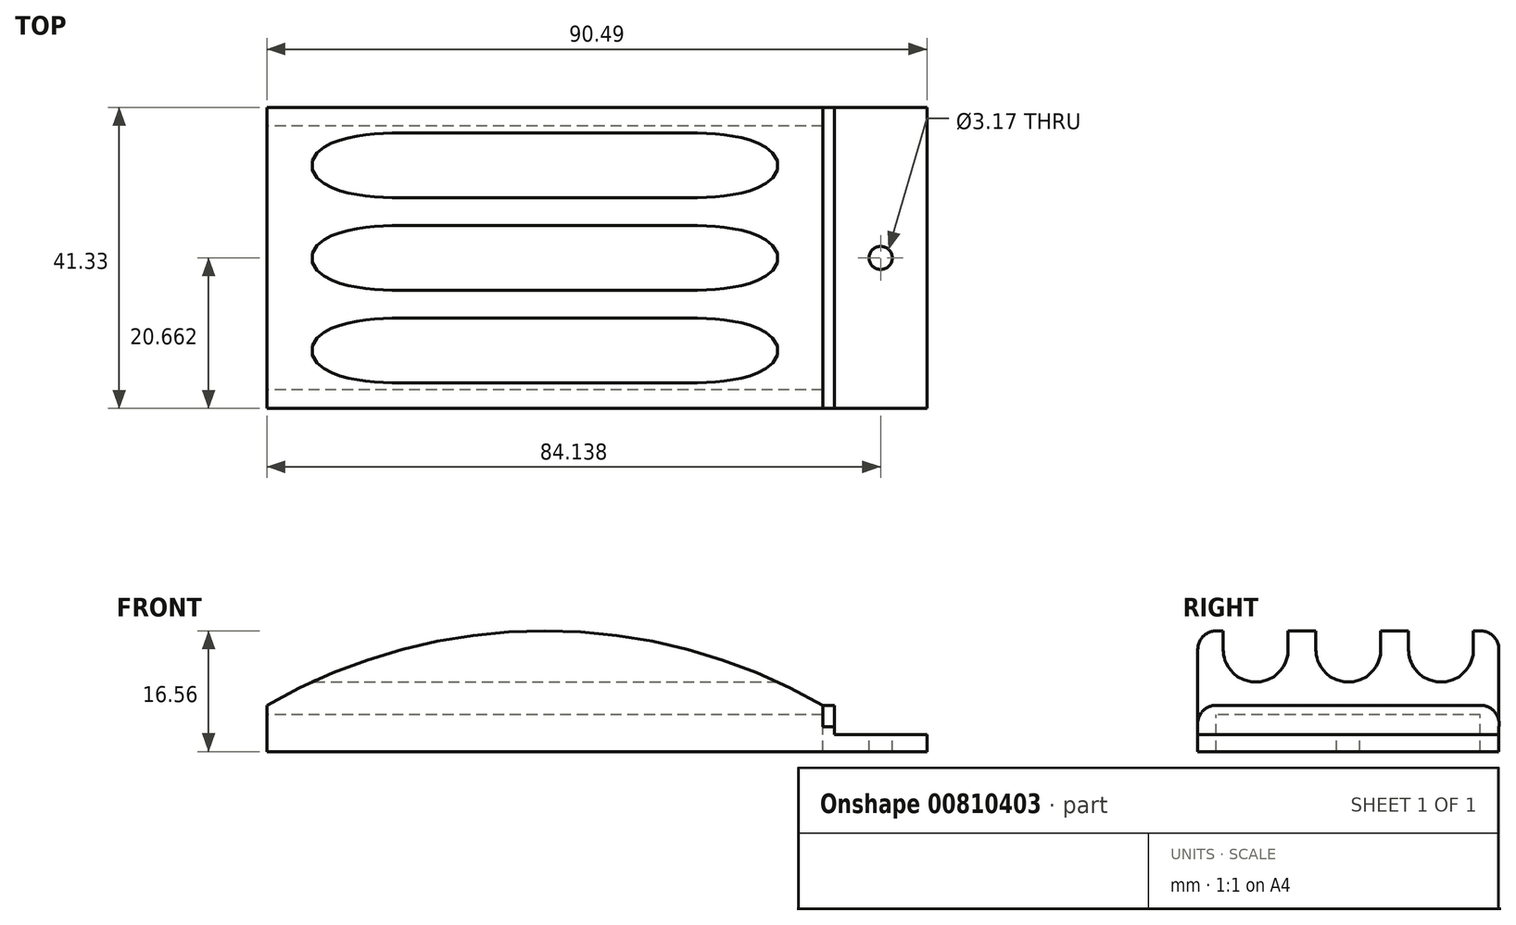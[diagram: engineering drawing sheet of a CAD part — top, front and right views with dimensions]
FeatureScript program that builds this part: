
annotation { "Feature Type Name" : "Feature", "Feature Type Description" : "" }
export const myFeature = defineFeature(function(context is Context, id is Id, definition is map)
    precondition{}
    {
        {
            var Q0;
            Q0=qCreatedBy(makeId("Front.planeOp"),FACE);
            var sketch = newSketch(context, id + "F0", { "sketchPlane" : qUnion([Q0])});
            skLineSegment(sketch, "E0", {"start": v(0, 0) * mm, "end": v(76.2, 0) * mm});
            skLineSegment(sketch, "E1", {"start": v(0, 0) * mm, "end": v(0, 6.35) * mm});
            skLineSegment(sketch, "E2", {"start": v(76.2, 0) * mm, "end": v(76.2, 6.35) * mm});
            skArc(sketch, "E3", {"start": v(76.2, 6.35) * mm, "mid": v(38.1, 16.56) * mm, "end": v(0, 6.35) * mm});
            skSolve(sketch);
        }
        {
            var Q0;
            Q0 = qSketchRegion(id + "F0", true);
            extrude(context, id + "F1", {"entities" : qUnion([Q0]), "depth" : 41.27 * mm, "offsetDistance" : 25.4 * mm});
        }
        {
            var Q0;
            Q0=makeQuery(id+"F1.opExtrude","SWEPT_FACE",FACE,{"disambiguationData":[OSD([sQuery(id+"F0.wireOp",EDGE,"E1")])]});
            var sketch = newSketch(context, id + "F2", { "sketchPlane" : qUnion([Q0])});
            skLineSegment(sketch, "E4.bottom", {"start": v(2.54, 0) * mm, "end": v(38.74, 0) * mm});
            skLineSegment(sketch, "E5.0", {"start": v(2.54, 0) * mm, "end": v(2.54, 5.08) * mm});
            skLineSegment(sketch, "E6.0", {"start": v(38.74, 0) * mm, "end": v(38.74, 5.08) * mm});
            skLineSegment(sketch, "E7.0", {"start": v(2.54, 5.08) * mm, "end": v(38.74, 5.08) * mm});
            skSolve(sketch);
        }
        {
            var Q0;
            Q0 = qSketchRegion(id + "F2", true);
            extrude(context, id + "F3", {"entities" : qUnion([Q0]), "operationType" : NewBodyOperationType.REMOVE, "endBound" : BoundingType.THROUGH_ALL, "oppositeDirection" : true, "depth" : 25.4 * mm, "offsetDistance" : 25.4 * mm});
        }
        {
            var Q0;
            Q0=makeQuery(id+"F1.opExtrude","CAP_EDGE",EDGE,{"disambiguationData":[OSD([sQuery(id+"F0.wireOp",EDGE,"E3")])],"isStart":true});
            fillet(context, id + "F4", {"entities" : qUnion([Q0]), "radius" : 2.54 * mm, "tangentPropagation" : true, "allowEdgeOverflow" : false});
        }
        {
            var Q0;
            Q0=makeQuery(id+"F1.opExtrude","CAP_EDGE",EDGE,{"disambiguationData":[OSD([sQuery(id+"F0.wireOp",EDGE,"E3")])],"isStart":false});
            fillet(context, id + "F5", {"entities" : qUnion([Q0]), "radius" : 2.54 * mm, "tangentPropagation" : true, "allowEdgeOverflow" : false});
        }
        {
            var Q0;
            Q0=makeQuery(id+"F1.opExtrude","SWEPT_FACE",FACE,{"disambiguationData":[OSD([sQuery(id+"F0.wireOp",EDGE,"E1")])]});
            var sketch = newSketch(context, id + "F6", { "sketchPlane" : qUnion([Q0])});
            skArc(sketch, "E8.0.startCap", {"start": v(12.38, 13.97) * mm, "mid": v(7.94, 9.53) * mm, "end": v(3.5, 13.97) * mm});
            skArc(sketch, "E8.0.endCap", {"start": v(3.5, 19.2) * mm, "mid": v(7.94, 23.64) * mm, "end": v(12.38, 19.2) * mm});
            skLineSegment(sketch, "E8.0.left", {"start": v(3.5, 13.97) * mm, "end": v(3.5, 19.2) * mm});
            skLineSegment(sketch, "E8.0.right", {"start": v(12.38, 13.97) * mm, "end": v(12.38, 19.2) * mm});
            skArc(sketch, "E9.0.startCap", {"start": v(25.08, 13.97) * mm, "mid": v(20.64, 9.53) * mm, "end": v(16.2, 13.97) * mm});
            skArc(sketch, "E9.0.endCap", {"start": v(16.2, 19.2) * mm, "mid": v(20.64, 23.64) * mm, "end": v(25.08, 19.2) * mm});
            skLineSegment(sketch, "E9.0.left", {"start": v(16.2, 13.97) * mm, "end": v(16.2, 19.2) * mm});
            skLineSegment(sketch, "E9.0.right", {"start": v(25.08, 13.97) * mm, "end": v(25.08, 19.2) * mm});
            skArc(sketch, "E10.0.startCap", {"start": v(37.78, 13.97) * mm, "mid": v(33.34, 9.53) * mm, "end": v(28.9, 13.97) * mm});
            skArc(sketch, "E10.0.endCap", {"start": v(28.9, 19.2) * mm, "mid": v(33.34, 23.64) * mm, "end": v(37.78, 19.2) * mm});
            skLineSegment(sketch, "E10.0.left", {"start": v(28.9, 13.97) * mm, "end": v(28.9, 19.2) * mm});
            skLineSegment(sketch, "E10.0.right", {"start": v(37.78, 13.97) * mm, "end": v(37.78, 19.2) * mm});
            skSolve(sketch);
        }
        {
            var Q0;
            Q0 = qSketchRegion(id + "F6", true);
            extrude(context, id + "F7", {"entities" : qUnion([Q0]), "operationType" : NewBodyOperationType.REMOVE, "endBound" : BoundingType.THROUGH_ALL, "oppositeDirection" : true, "depth" : 25.4 * mm, "offsetDistance" : 25.4 * mm});
        }
        {
            var Q0;
            Q0=makeQuery(id+"F1.opExtrude","SWEPT_FACE",FACE,{"disambiguationData":[OSD([sQuery(id+"F0.wireOp",EDGE,"E2")])]});
            var sketch = newSketch(context, id + "F8", { "sketchPlane" : qUnion([Q0])});
            skLineSegment(sketch, "E11", {"start": v(-41.28, 3.4) * mm, "end": v(-41.28, 0) * mm});
            skLineSegment(sketch, "E12", {"start": v(-41.28, 0) * mm, "end": v(0, 0) * mm});
            skLineSegment(sketch, "E13", {"start": v(0, 0) * mm, "end": v(0, 3.4) * mm});
            skLineSegment(sketch, "E14", {"start": v(-38.74, 6.35) * mm, "end": v(-2.54, 6.35) * mm});
            skArc(sketch, "E15", {"start": v(-38.74, 6.35) * mm, "mid": v(-40.68, 5.46) * mm, "end": v(-41.28, 3.4) * mm});
            skArc(sketch, "E16", {"start": v(0, 3.4) * mm, "mid": v(-0.6, 5.46) * mm, "end": v(-2.54, 6.35) * mm});
            skSolve(sketch);
        }
        {
            var Q0;
            Q0 = qSketchRegion(id + "F8", true);
            extrude(context, id + "F9", {"entities" : qUnion([Q0]), "operationType" : NewBodyOperationType.ADD, "depth" : 1.59 * mm, "offsetDistance" : 25.4 * mm});
        }
        {
            var Q0;
            Q0=makeQuery(id+"F9.opExtrude","CAP_FACE",FACE,{"disambiguationData":[OSD([sQuery(id+"F8.wireOp",EDGE,"E11"),sQuery(id+"F8.wireOp",EDGE,"E12"),sQuery(id+"F8.wireOp",EDGE,"E13"),sQuery(id+"F8.wireOp",EDGE,"E14"),sQuery(id+"F8.wireOp",EDGE,"E15"),sQuery(id+"F8.wireOp",EDGE,"E16")])],"isStart":false});
            var sketch = newSketch(context, id + "F10", { "sketchPlane" : qUnion([Q0])});
            skLineSegment(sketch, "E17.bottom", {"start": v(-41.28, 0) * mm, "end": v(0, 0) * mm});
            skLineSegment(sketch, "E17.top", {"start": v(-41.28, 2.3) * mm, "end": v(0, 2.3) * mm});
            skLineSegment(sketch, "E17.left", {"start": v(-41.28, 0) * mm, "end": v(-41.28, 2.3) * mm});
            skLineSegment(sketch, "E17.right", {"start": v(0, 0) * mm, "end": v(0, 2.3) * mm});
            skSolve(sketch);
        }
        {
            var Q0;
            Q0 = qSketchRegion(id + "F10", true);
            extrude(context, id + "F11", {"entities" : qUnion([Q0]), "operationType" : NewBodyOperationType.ADD, "depth" : 12.7 * mm, "offsetDistance" : 25.4 * mm});
        }
        {
            var Q0;
            Q0=makeQuery(id+"F11.opExtrude","SWEPT_FACE",FACE,{"disambiguationData":[OSD([sQuery(id+"F10.wireOp",EDGE,"E17.top")])]});
            var sketch = newSketch(context, id + "F12", { "sketchPlane" : qUnion([Q0])});
            skCircle(sketch, "E18", {"center": v(84.14, -20.64) * mm, "radius": 1.59 * mm});
            skSolve(sketch);
        }
        {
            var Q0;
            Q0=makeQuery(id+"F12.imprint","IMPRINT",FACE,{"disambiguationData":[TD([[makeQuery(id+"F12.imprint","IMPRINT",EDGE,{"derivedFrom":sQuery(id+"F12.wireOp",EDGE,"E18")}),1.0]])]});
            var Q1;
            Q1=sQuery(id+"F12.wireOp",EDGE,"E18");
            extrude(context, id + "F13", {"entities" : qUnion([Q0]), "operationType" : NewBodyOperationType.REMOVE, "surfaceEntities" : qUnion([Q1]), "endBound" : BoundingType.THROUGH_ALL, "oppositeDirection" : true, "depth" : 25.4 * mm, "offsetDistance" : 25.4 * mm});
        }
    });
